# Revit family: NBS_WallgateLtd_WlHngWshBsns_ALS-1802
name_source: partatom
category: Plumbing Fixtures
revit_build: Autodesk Revit 2014 (Build: 20130709_2115(x64)
units: mm (PartAtom-declared; Revit-internal decimal feet)

## types (1)
- ALS-180
    ActivationOptions = Piezo touch buttons or Infra red sensor
    AssetType = Fixed
    BIMObjectName = NBS_WallgateLtd_WallHungWashBasins_ALS-180
    CloseOffRating = 0
    ColourOptions = MA - Thames, MAH - Frost, MAW - White, MC - Bluestone, MCA - Aubergine, MCB - Diamantina, MCC - Black, MCD - Orange, MCE - Pink, MO - Slate, MS - Hyco, MCJ - Light Grey, MCF - NHS Blue
    Description = Anti-Ligature, anti-vandal solid surface basin with dual outlets and piezo/ infra-red activation, with MOJ Safer Cell approval
    DrainSize = 32 mm
    Durability = Compliant to Grade 5
    DurationUnit = year
    FaucetFunction = Mixed
    FaucetOperation = TimedSelfClosing
    FaucetTopDescription = Unset
    FaucetType = Other
    Features = Hygienic and easily cleaned, highly vandal-resistant
    FixingMaterial = NBS_Concept
    FlowCoefficient = 0
    IfcExportAs = IfcSanitaryTerminalType
    IfcExportType = WASHHANDBASIN
    IntegralAccessoryOptions = WDC Electronic Controllers, WVPB Basin Water Valve Pack, MV0001 Thermostatic Mixer Valve, MBS Manifold
    ManufacturerName = Wallgate Ltd
    ManufacturerURL = www.wallgate.com
    Material = High-grade solid surface material
    ModelNumber = ALS-180
    NBSCertification = www.nationalbimlibrary.com/cert/kigsdpbw
    NBSDescription = Wall hung wash basins
    NBSReference = 45-35-70/369
    Name = WallHungWashBasins_ALS-180_WallgateLtd
    NominalDepth = 300 mm
    NominalHeight = 450 mm  [stored 1.47638 ft]
    NominalLength = 0 mm  [stored 0 ft]
    NominalWidth = 470 mm  [stored 1.54199 ft]
    OutletOptions = Single or Dual outlets
    ProductInformation = www.wallgate.com/products/wash-basins/als-secure-basin-range
    Size = 15.0
    Standard = BS EN14688
    TestPressure = 0.0
    Uniclass2 = 45-31-79/494
    ValveMechanism = Unset
    ValveOperation = Other
    ValvePattern = Unset
    Version = 1
    WallThicknessOptions = 10-85 mm, 85-190 mm
    WarrantyDurationParts = 1
    WarrantyDurationUnit = year
    WashBasinMaterial = NBS_Concept
    WashHandBasinMounting = WallHung
    WashHandBasinType = HandRinse
    WaterSupplyFittingMaterial = NBS_Concept
    WaterSupplyOverflowAndWasteHolesOverflow = None
    WaterSupplyOverflowAndWasteHolesWaste = Bottom waste outlet
    Weight = 18.5 kg
    WorkingPressure = 0

note: [stored X ft] marks values corroborated as IEEE doubles in the binary element streams (Revit-internal decimal feet)

## geometry (parser evidence)
native form markers: Sweep x6
no freeform markers — native parametric forms only
